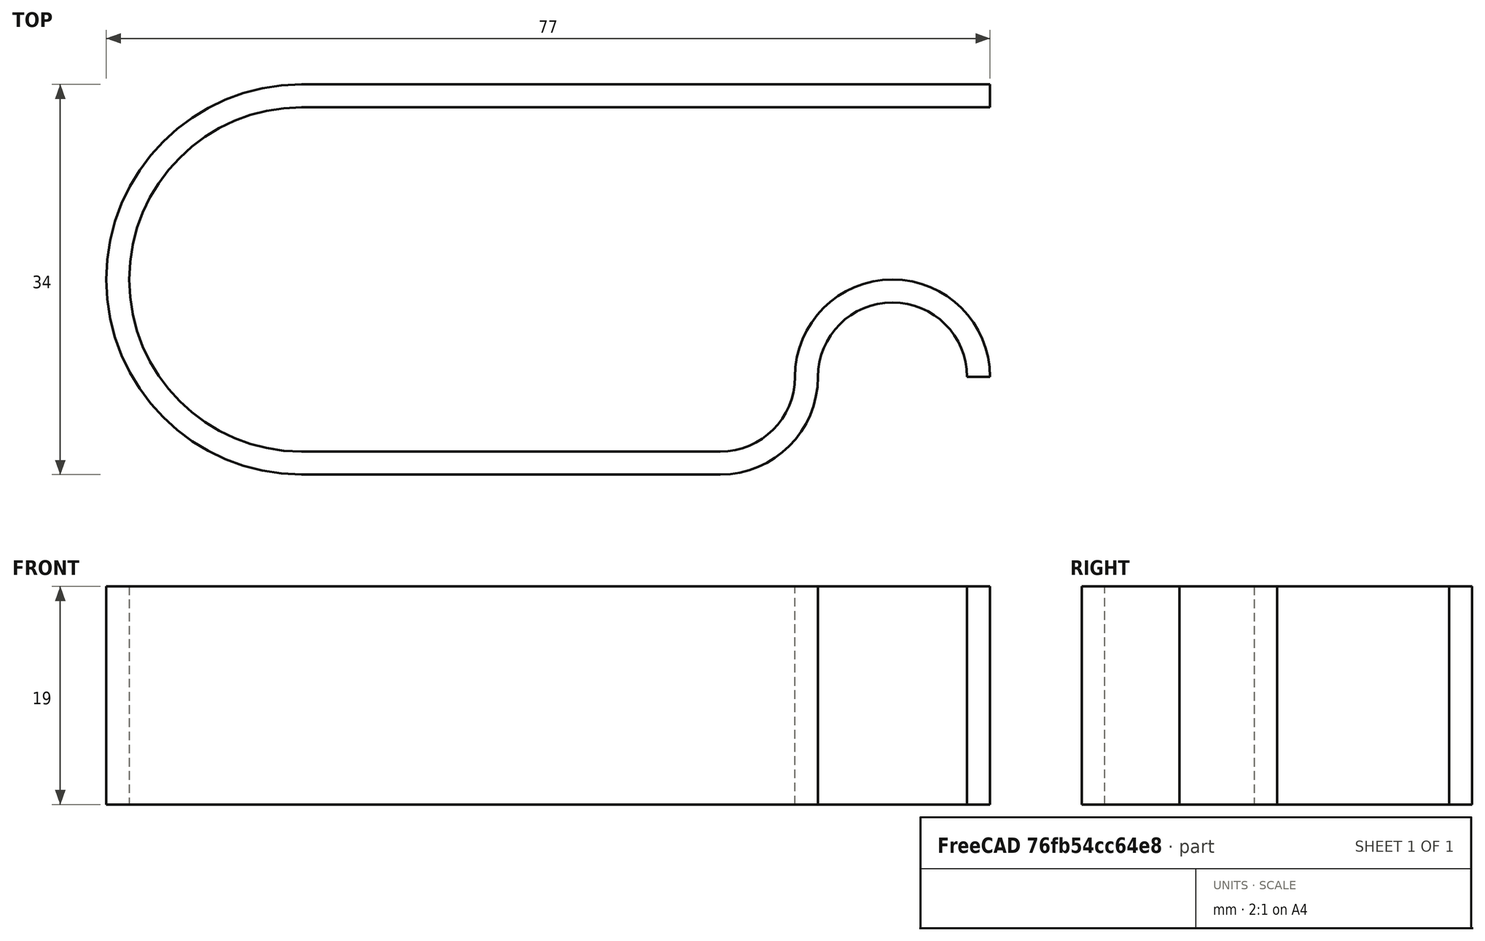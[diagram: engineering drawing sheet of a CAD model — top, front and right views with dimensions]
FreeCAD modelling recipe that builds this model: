
FCSTD DOCUMENT  (FreeCAD 0.20R29603 (Git))
Label: Cable Clip
License: All rights reserved
LicenseURL: http://en.wikipedia.org/wiki/All_rights_reserved
objects: Spreadsheet::Sheet×1, Sketcher::SketchObject×1, PartDesign::Pad×1, PartDesign::Body×1, App::Part×1
note: 4 computed .brp shape members not serialized (recipe doc carries the construction recipe); baked Part::Feature solids carry a one-line shape summary decoded from their .brp

FEATURE [Spreadsheet::Sheet] Spreadsheet  label="Parameters"
  cells = A1=length; B1(length)=60; A2=height; B2(height)=30; A3=width; B3(width)=19; A4=wall_thickness; B4(wall_thickness)=2; A5=grip_factor; B5(grip_factor)=0.5
FEATURE [Sketcher::SketchObject] Sketch
  FullyConstrained = true
  MapMode = 5
  expr: Constraints[14] = Spreadsheet.height / 2 + Spreadsheet.wall_thickness
  expr: Constraints[15] = Spreadsheet.height / 2
  expr: Constraints[34] = max(Spreadsheet.length; 3 * Spreadsheet.height * Spreadsheet.grip_factor / 2 + Spreadsheet.wall_thickness)
  expr: Constraints[36] = max(Spreadsheet.height * Spreadsheet.grip_factor / 2 + Spreadsheet.wall_thickness / 2; Spreadsheet.wall_thickness * 1.1)
  expr: Constraints[37] = max(Spreadsheet.height * Spreadsheet.grip_factor / 2 + Spreadsheet.wall_thickness / 2; Spreadsheet.wall_thickness * 1.1)
  sketch-geometry (12):
    g0: LineSegment StartX=0 StartY=0 StartZ=0 EndX=-60 EndY=0 EndZ=0
    g1: ArcOfCircle CenterX=-60 CenterY=-15 CenterZ=0 NormalX=0 NormalY=0 NormalZ=1 AngleXU=0 Radius=15 StartAngle=1.5708 EndAngle=4.71239
    g2: ArcOfCircle CenterX=-60 CenterY=-15 CenterZ=0 NormalX=0 NormalY=0 NormalZ=1 AngleXU=0 Radius=17 StartAngle=1.5708 EndAngle=4.71239
    g3: LineSegment StartX=-60 StartY=2 StartZ=0 EndX=0 EndY=2 EndZ=0
    g4: LineSegment StartX=-60 StartY=-32 StartZ=0 EndX=-23.5 EndY=-32 EndZ=0
    g5: LineSegment StartX=-60 StartY=-30 StartZ=0 EndX=-23.5 EndY=-30 EndZ=0
    g6: LineSegment StartX=0 StartY=2 StartZ=0 EndX=0 EndY=0 EndZ=0
    g7: ArcOfCircle CenterX=-23.5 CenterY=-23.5 CenterZ=0 NormalX=0 NormalY=0 NormalZ=1 AngleXU=0 Radius=6.5 StartAngle=4.71239 EndAngle=6.28319
    g8: ArcOfCircle CenterX=-23.5 CenterY=-23.5 CenterZ=0 NormalX=0 NormalY=0 NormalZ=1 AngleXU=0 Radius=8.5 StartAngle=4.71239 EndAngle=6.28319
    g9: ArcOfCircle CenterX=-8.5 CenterY=-23.5 CenterZ=0 NormalX=0 NormalY=0 NormalZ=1 AngleXU=0 Radius=6.5 StartAngle=0 EndAngle=3.14159
    g10: ArcOfCircle CenterX=-8.5 CenterY=-23.5 CenterZ=0 NormalX=0 NormalY=0 NormalZ=1 AngleXU=0 Radius=8.5 StartAngle=0 EndAngle=3.14159
    g11: LineSegment StartX=0 StartY=-23.5 StartZ=0 EndX=-2 EndY=-23.5 EndZ=0
  constraints (38):
    c: Coincident(g1,g0)
    c: Coincident(g2,g1)
    c: Coincident(g3,g2)
    c: Parallel(g3,g0)
    c: Coincident(g4,g2)
    c: Coincident(g5,g1)
    c: Horizontal(g5)
    c: Parallel(g4,g5)
    c: Coincident(g6,g3)
    c: Coincident(g6,g0)
    c: Vertical(g5,g4)
    c: Vertical(g0,g2)
    c: Vertical(g2,g2)
    c: Vertical(g2,g1)
    c: Radius(g2) = 17
    c: Radius(g1) = 15
    c: Horizontal(g0)
    c: Vertical(g0,g3)
    c: Coincident(g7,g5)
    c: Vertical(g7,g5)
    c: Horizontal(g7,g7)
    c: Coincident(g8,g7)
    c: Coincident(g8,g4)
    c: Horizontal(g7,g8)
    c: Coincident(g9,g8)
    c: Horizontal(g9,g7)
    c: Horizontal(g9,g7)
    c: Coincident(g10,g9)
    c: Coincident(g10,g7)
    c: Horizontal(g10,g7)
    c: Coincident(g11,g10)
    c: Coincident(g11,g9)
    c: Vertical(g1,g2)
    c: Vertical(g10,g0)
    c: DistanceX(g2,g3) = 60
    c: Coincident(g-1,g0)
    c: Radius(g8) = 8.5
    c: Radius(g10) = 8.5
FEATURE [PartDesign::Pad] Pad  label="Cable Clip001"
  Direction = (0,0,1)
  Length = 19
  Length2 = 10
  Profile = -> Sketch
  ReferenceAxis = -> Sketch [N_Axis]
  Type = 0
  expr: Length = <<Parameters>>.width
FEATURE [PartDesign::Body] Body
  Group = -> [Sketch,Pad]
  Origin = -> Origin001
  Tip = -> Pad
FEATURE [App::Part] Part  label="Cable Clip"
  Group = -> [Body]
  Origin = -> Origin
